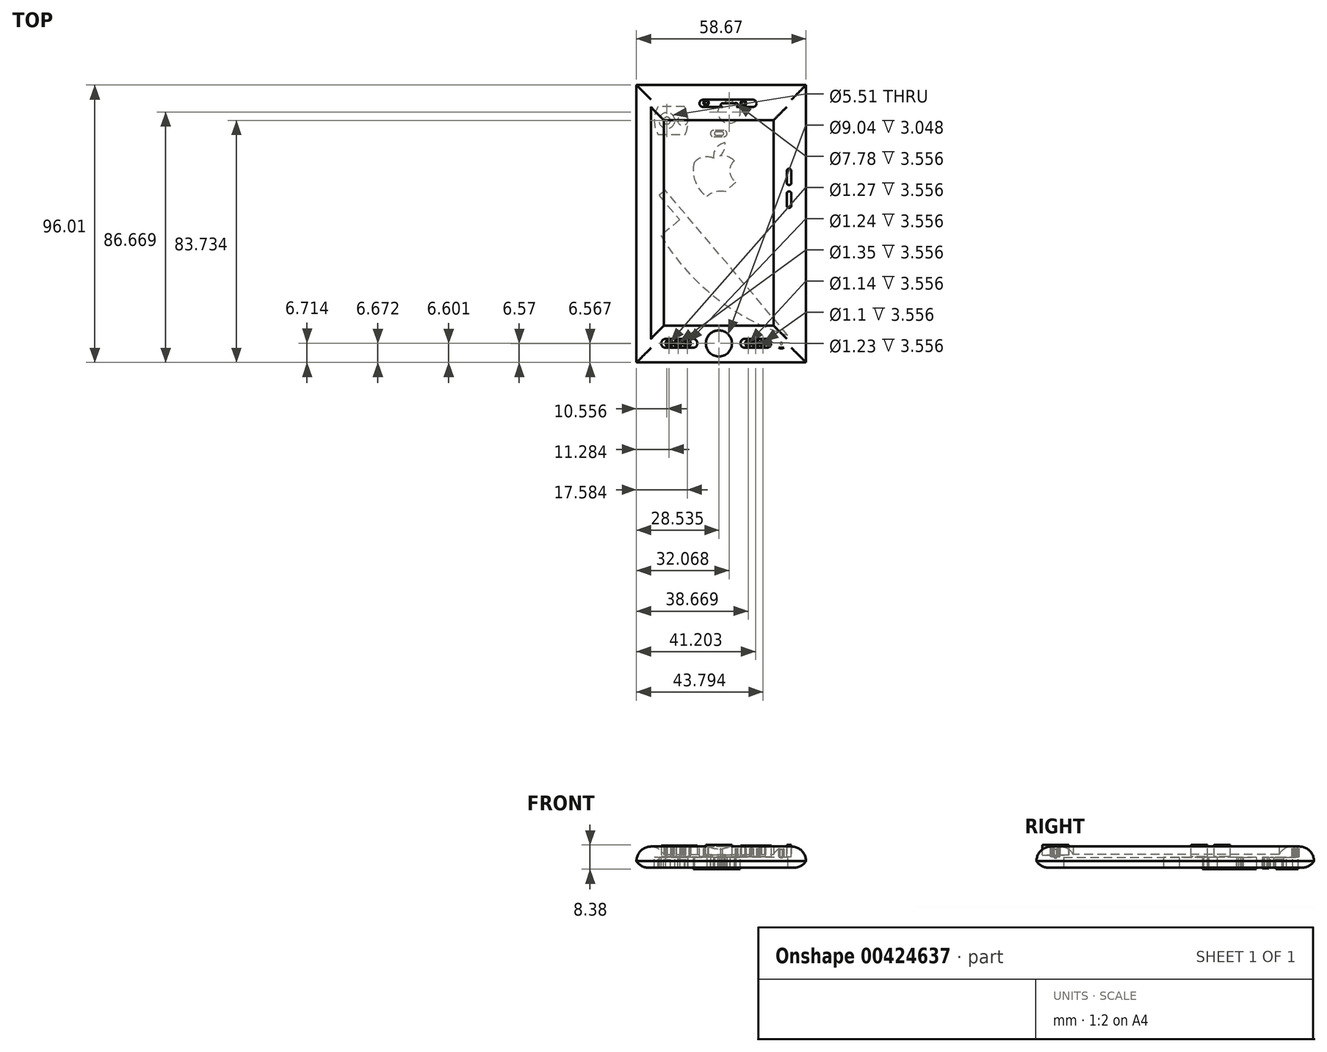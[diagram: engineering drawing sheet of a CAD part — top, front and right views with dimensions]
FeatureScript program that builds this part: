
annotation { "Feature Type Name" : "Feature", "Feature Type Description" : "" }
export const myFeature = defineFeature(function(context is Context, id is Id, definition is map)
    precondition{}
    {
        {
            var Q0;
            Q0=qCreatedBy(makeId("Top.planeOp"),FACE);
            var sketch = newSketch(context, id + "F0", { "sketchPlane" : qUnion([Q0])});
            skLineSegment(sketch, "E0", {"start": v(31.94, 80.74) * mm, "end": v(31.94, -15.27) * mm});
            skLineSegment(sketch, "E1", {"start": v(-26.73, 80.74) * mm, "end": v(-26.73, -15.27) * mm});
            skLineSegment(sketch, "E2", {"start": v(-26.73, -15.27) * mm, "end": v(31.94, -15.27) * mm});
            skLineSegment(sketch, "E3", {"start": v(31.94, 80.74) * mm, "end": v(-26.73, 80.74) * mm});
            skSolve(sketch);
        }
        {
            var Q0;
            Q0=makeQuery(id+"F0.imprint","IMPRINT",FACE,{"disambiguationData":[TD([[makeQuery(id+"F0.imprint","IMPRINT",EDGE,{"derivedFrom":sQuery(id+"F0.wireOp",EDGE,"E0")}),-1.0]])]});
            extrude(context, id + "F1", {"entities" : qUnion([Q0]), "depth" : 7.37 * mm});
        }
        {
            var Q0;
            Q0=makeQuery(id+"F1.opExtrude","CAP_FACE",FACE,{"disambiguationData":[OSD([sQuery(id+"F0.wireOp",EDGE,"E0"),sQuery(id+"F0.wireOp",EDGE,"E1"),sQuery(id+"F0.wireOp",EDGE,"E2"),sQuery(id+"F0.wireOp",EDGE,"E3")])],"isStart":false});
            var sketch = newSketch(context, id + "F2", { "sketchPlane" : qUnion([Q0])});
            skLineSegment(sketch, "E4.bottom", {"start": v(-17.26, 68.64) * mm, "end": v(20.73, 68.64) * mm});
            skLineSegment(sketch, "E4.top", {"start": v(-17.26, -2.55) * mm, "end": v(20.73, -2.55) * mm});
            skLineSegment(sketch, "E4.left", {"start": v(-17.26, 68.64) * mm, "end": v(-17.26, -2.55) * mm});
            skLineSegment(sketch, "E4.right", {"start": v(20.73, 68.64) * mm, "end": v(20.73, -2.55) * mm});
            skSolve(sketch);
        }
        {
            var Q0;
            Q0=makeQuery(id+"F2.imprint","IMPRINT",FACE,{"disambiguationData":[TD([[makeQuery(id+"F2.imprint","IMPRINT",EDGE,{"derivedFrom":sQuery(id+"F2.wireOp",EDGE,"E4.bottom")}),-1.0]])]});
            extrude(context, id + "F3", {"entities" : qUnion([Q0]), "operationType" : NewBodyOperationType.REMOVE, "oppositeDirection" : true, "depth" : 2.8 * mm});
        }
        {
            var Q0;
            Q0=makeQuery(id+"F3.boolean.opBoolean","COPY",FACE,{"derivedFrom":makeQuery(id+"F3.opExtrude","CAP_FACE",FACE,{"disambiguationData":[OSD([sQuery(id+"F2.wireOp",EDGE,"E4.bottom"),sQuery(id+"F2.wireOp",EDGE,"E4.top"),sQuery(id+"F2.wireOp",EDGE,"E4.left"),sQuery(id+"F2.wireOp",EDGE,"E4.right")])],"isStart":false})});
            extrude(context, id + "F4", {"entities" : qUnion([Q0]), "depth" : 2.8 * mm});
        }
        {
            var Q0;
            Q0=makeQuery(id+"F1.opExtrude","CAP_FACE",FACE,{"disambiguationData":[OSD([sQuery(id+"F0.wireOp",EDGE,"E0"),sQuery(id+"F0.wireOp",EDGE,"E1"),sQuery(id+"F0.wireOp",EDGE,"E2"),sQuery(id+"F0.wireOp",EDGE,"E3")])],"isStart":false});
            fillet(context, id + "F5", {"entities" : qUnion([Q0]), "radius" : 5.08 * mm, "tangentPropagation" : true, "allowEdgeOverflow" : false});
        }
        {
            var Q0;
            Q0=makeQuery(id+"F1.opExtrude","CAP_FACE",FACE,{"disambiguationData":[OSD([sQuery(id+"F0.wireOp",EDGE,"E0"),sQuery(id+"F0.wireOp",EDGE,"E1"),sQuery(id+"F0.wireOp",EDGE,"E2"),sQuery(id+"F0.wireOp",EDGE,"E3")])],"isStart":true});
            fillet(context, id + "F6", {"entities" : qUnion([Q0]), "radius" : 5.08 * mm, "tangentPropagation" : true, "allowEdgeOverflow" : false});
        }
        {
            var Q0;
            Q0=makeQuery(id+"F1.opExtrude","CAP_FACE",FACE,{"disambiguationData":[OSD([sQuery(id+"F0.wireOp",EDGE,"E0"),sQuery(id+"F0.wireOp",EDGE,"E1"),sQuery(id+"F0.wireOp",EDGE,"E2"),sQuery(id+"F0.wireOp",EDGE,"E3")])],"isStart":false});
            var sketch = newSketch(context, id + "F7", { "sketchPlane" : qUnion([Q0])});
            skCircle(sketch, "E5", {"center": v(1.8, -8.67) * mm, "radius": 4.52 * mm});
            skSolve(sketch);
        }
        {
            var Q0;
            Q0 = qSketchRegion(id + "F7", true);
            extrude(context, id + "F8", {"entities" : qUnion([Q0]), "operationType" : NewBodyOperationType.REMOVE, "oppositeDirection" : true, "depth" : 3.05 * mm});
        }
        {
            var Q0;
            Q0=makeQuery(id+"F8.boolean.opBoolean","COPY",FACE,{"derivedFrom":makeQuery(id+"F8.opExtrude","CAP_FACE",FACE,{"disambiguationData":[OSD([sQuery(id+"F7.wireOp",EDGE,"E5")])],"isStart":false})});
            extrude(context, id + "F9", {"entities" : qUnion([Q0]), "depth" : 3.56 * mm});
        }
        {
            var Q0;
            Q0=makeQuery(id+"F1.opExtrude","CAP_FACE",FACE,{"disambiguationData":[OSD([sQuery(id+"F0.wireOp",EDGE,"E0"),sQuery(id+"F0.wireOp",EDGE,"E1"),sQuery(id+"F0.wireOp",EDGE,"E2"),sQuery(id+"F0.wireOp",EDGE,"E3")])],"isStart":true});
            var sketch = newSketch(context, id + "F10", { "sketchPlane" : qUnion([Q0])});
            skLineSegment(sketch, "E6", {"start": v(25.58, 5.84) * mm, "end": v(4.61, -18.99) * mm});
            skLineSegment(sketch, "E7", {"start": v(4.61, -18.99) * mm, "end": v(-4.3, -29.54) * mm});
            skLineSegment(sketch, "E8", {"start": v(-4.3, -29.54) * mm, "end": v(-9.77, -36.03) * mm});
            skLineSegment(sketch, "E9", {"start": v(-9.77, -36.03) * mm, "end": v(-16.77, -44.32) * mm});
            skLineSegment(sketch, "E10", {"start": v(-16.77, -44.32) * mm, "end": v(-18.9, -42.52) * mm});
            skLineSegment(sketch, "E11", {"start": v(-18.9, -42.52) * mm, "end": v(-11.81, -34.13) * mm});
            skLineSegment(sketch, "E12", {"start": v(-11.81, -34.13) * mm, "end": v(-18.28, -28.67) * mm});
            skArc(sketch, "E13", {"start": v(25.58, 5.84) * mm, "mid": v(0.46, -7.36) * mm, "end": v(-18.28, -28.67) * mm});
            skSolve(sketch);
        }
        {
            var Q0;
            Q0 = qSketchRegion(id + "F10", true);
            extrude(context, id + "F11", {"entities" : qUnion([Q0]), "operationType" : NewBodyOperationType.REMOVE, "oppositeDirection" : true, "depth" : 3.56 * mm});
        }
        {
            var Q0;
            Q0=makeQuery(id+"F11.boolean.opBoolean","COPY",FACE,{"derivedFrom":makeQuery(id+"F11.opExtrude","CAP_FACE",FACE,{"disambiguationData":[OSD([sQuery(id+"F10.wireOp",EDGE,"E6"),sQuery(id+"F10.wireOp",EDGE,"E7"),sQuery(id+"F10.wireOp",EDGE,"E8"),sQuery(id+"F10.wireOp",EDGE,"E9"),sQuery(id+"F10.wireOp",EDGE,"E10"),sQuery(id+"F10.wireOp",EDGE,"E11"),sQuery(id+"F10.wireOp",EDGE,"E12"),sQuery(id+"F10.wireOp",EDGE,"E13")])],"isStart":false})});
            extrude(context, id + "F12", {"entities" : qUnion([Q0]), "depth" : 3.56 * mm});
        }
        {
            var Q0;
            Q0=qCreatedBy(makeId("Top.planeOp"),FACE);
            var sketch = newSketch(context, id + "F13", { "sketchPlane" : qUnion([Q0])});
            skArc(sketch, "E14", {"start": v(7.09, 54.53) * mm, "mid": v(5.57, 50.71) * mm, "end": v(7.7, 47.2) * mm});
            skArc(sketch, "E15", {"start": v(7.09, 54.53) * mm, "mid": v(3.7, 56.23) * mm, "end": v(0, 55.38) * mm});
            skArc(sketch, "E16", {"start": v(0, 55.38) * mm, "mid": v(-3.61, 55.8) * mm, "end": v(-6.74, 53.95) * mm});
            skArc(sketch, "E17", {"start": v(-6.74, 53.95) * mm, "mid": v(-6.38, 47.38) * mm, "end": v(-2.37, 42.16) * mm});
            skArc(sketch, "E18", {"start": v(3.93, 43.83) * mm, "mid": v(0.57, 43.76) * mm, "end": v(-2.37, 42.16) * mm});
            skLineSegment(sketch, "E19", {"start": v(7.7, 47.2) * mm, "end": v(3.93, 43.83) * mm});
            skArc(sketch, "E20", {"start": v(0, 55.38) * mm, "mid": v(3.12, 57.25) * mm, "end": v(3.87, 60.8) * mm});
            skArc(sketch, "E21", {"start": v(3.87, 60.8) * mm, "mid": v(0.85, 58.87) * mm, "end": v(0, 55.38) * mm});
            skSolve(sketch);
        }
        {
            var Q0;
            {var subQ0=sQuery(id+"F13.wireOp",EDGE,"E21");Q0=makeQuery(id+"F13.imprint","IMPRINT",FACE,{"disambiguationData":[TD([[makeQuery(id+"F13.imprint","IMPRINT",EDGE,{"derivedFrom":subQ0}),1.0]])]});}
            var Q1;
            {var subQ0=sQuery(id+"F13.wireOp",EDGE,"E20");var subQ1=sQuery(id+"F13.wireOp",EDGE,"E15");var subQ3=makeQuery(id+"F13.imprint","INTERSECT",VERTEX,{"derivedFrom":[subQ1,subQ0]});Q1=makeQuery(id+"F13.imprint","IMPRINT",FACE,{"disambiguationData":[TD([[makeQuery(id+"F13.imprint","IMPRINT",EDGE,{"disambiguationData":[TD([[subQ3,-1.0]])],"derivedFrom":subQ1}),1.0]])]});}
            var Q2;
            {var subQ2=sQuery(id+"F13.wireOp",EDGE,"E14");Q2=makeQuery(id+"F13.imprint","IMPRINT",FACE,{"disambiguationData":[TD([[makeQuery(id+"F13.imprint","IMPRINT",EDGE,{"derivedFrom":subQ2}),-1.0]])]});}
            extrude(context, id + "F14", {"entities" : qUnion([Q0, Q1, Q2]), "operationType" : NewBodyOperationType.REMOVE, "depth" : 3.56 * mm});
        }
        {
            var Q0;
            Q0=makeQuery(id+"F14.boolean.opBoolean","COPY",FACE,{"derivedFrom":makeQuery(id+"F14.opExtrude","CAP_FACE",FACE,{"disambiguationData":[OSD([sQuery(id+"F13.wireOp",EDGE,"E14"),sQuery(id+"F13.wireOp",EDGE,"E15"),sQuery(id+"F13.wireOp",EDGE,"E16"),sQuery(id+"F13.wireOp",EDGE,"E17"),sQuery(id+"F13.wireOp",EDGE,"E18"),sQuery(id+"F13.wireOp",EDGE,"E19"),sQuery(id+"F13.wireOp",EDGE,"E20"),sQuery(id+"F13.wireOp",EDGE,"E21")])],"isStart":false})});
            extrude(context, id + "F15", {"entities" : qUnion([Q0]), "depth" : 4.06 * mm});
        }
        {
            var Q0;
            Q0=makeQuery(id+"F1.opExtrude","CAP_FACE",FACE,{"disambiguationData":[OSD([sQuery(id+"F0.wireOp",EDGE,"E0"),sQuery(id+"F0.wireOp",EDGE,"E1"),sQuery(id+"F0.wireOp",EDGE,"E2"),sQuery(id+"F0.wireOp",EDGE,"E3")])],"isStart":true});
            var sketch = newSketch(context, id + "F16", { "sketchPlane" : qUnion([Q0])});
            skLineSegment(sketch, "E22", {"start": v(-10.1, -73.34) * mm, "end": v(-19.28, -73.34) * mm});
            skArc(sketch, "E23", {"start": v(-19.28, -63.67) * mm, "mid": v(-20.55, -68.5) * mm, "end": v(-19.28, -73.34) * mm});
            skLineSegment(sketch, "E24", {"start": v(-19.28, -63.67) * mm, "end": v(-9.78, -63.67) * mm});
            skArc(sketch, "E25", {"start": v(-10.1, -73.34) * mm, "mid": v(-8.86, -68.49) * mm, "end": v(-9.88, -63.58) * mm});
            skCircle(sketch, "E26", {"center": v(-16.17, -68.46) * mm, "radius": 2.75 * mm});
            skCircle(sketch, "E27", {"center": v(-16.17, -68.46) * mm, "radius": 1.6 * mm});
            skCircle(sketch, "E28", {"center": v(-10.69, -68.5) * mm, "radius": 1.76 * mm});
            skSolve(sketch);
        }
        {
            var Q0;
            Q0 = qSketchRegion(id + "F16", true);
            extrude(context, id + "F17", {"entities" : qUnion([Q0]), "operationType" : NewBodyOperationType.REMOVE, "oppositeDirection" : true, "depth" : 3.56 * mm});
        }
        {
            var Q0;
            Q0=makeQuery(id+"F17.boolean.opBoolean","COPY",FACE,{"derivedFrom":makeQuery(id+"F17.opExtrude","CAP_FACE",FACE,{"disambiguationData":[OSD([sQuery(id+"F16.wireOp",EDGE,"E22"),sQuery(id+"F16.wireOp",EDGE,"E23"),sQuery(id+"F16.wireOp",EDGE,"E24"),sQuery(id+"F16.wireOp",EDGE,"E25"),sQuery(id+"F16.wireOp",EDGE,"E26"),sQuery(id+"F16.wireOp",EDGE,"E28")])],"isStart":false})});
            extrude(context, id + "F18", {"entities" : qUnion([Q0]), "depth" : 3.56 * mm});
        }
        {
            var Q0;
            Q0=makeQuery(id+"F17.boolean.opBoolean","SPLIT",FACE,{"disambiguationData":[TD([makeQuery(id+"F17.opExtrude","SWEPT_FACE",FACE,{"disambiguationData":[OSD([sQuery(id+"F16.wireOp",EDGE,"E26")])]})])],"derivedFrom":makeQuery(id+"F1.opExtrude","CAP_FACE",FACE,{"disambiguationData":[OSD([sQuery(id+"F0.wireOp",EDGE,"E0"),sQuery(id+"F0.wireOp",EDGE,"E1"),sQuery(id+"F0.wireOp",EDGE,"E2"),sQuery(id+"F0.wireOp",EDGE,"E3")])],"isStart":true})});
            var sketch = newSketch(context, id + "F19", { "sketchPlane" : qUnion([Q0])});
            skCircle(sketch, "E29", {"center": v(-16.17, -68.46) * mm, "radius": 1.23 * mm});
            skCircle(sketch, "E30", {"center": v(-10.43, -68.62) * mm, "radius": 1.64 * mm});
            skSolve(sketch);
        }
        {
            var Q0;
            Q0=makeQuery(id+"F19.imprint","IMPRINT",FACE,{"disambiguationData":[TD([[makeQuery(id+"F19.imprint","IMPRINT",EDGE,{"derivedFrom":sQuery(id+"F19.wireOp",EDGE,"E29")}),1.0]])]});
            extrude(context, id + "F20", {"entities" : qUnion([Q0]), "operationType" : NewBodyOperationType.REMOVE, "oppositeDirection" : true, "depth" : 2.8 * mm});
        }
        {
            var Q0;
            Q0=makeQuery(id+"F20.boolean.opBoolean","COPY",FACE,{"derivedFrom":makeQuery(id+"F20.opExtrude","CAP_FACE",FACE,{"disambiguationData":[OSD([sQuery(id+"F19.wireOp",EDGE,"E29")])],"isStart":false})});
            extrude(context, id + "F21", {"entities" : qUnion([Q0]), "depth" : 2.8 * mm});
        }
        {
            var Q0;
            Q0=makeQuery(id+"F17.boolean.opBoolean","SPLIT",FACE,{"disambiguationData":[TD([makeQuery(id+"F17.opExtrude","SWEPT_FACE",FACE,{"disambiguationData":[OSD([sQuery(id+"F16.wireOp",EDGE,"E28")])]})])],"derivedFrom":makeQuery(id+"F1.opExtrude","CAP_FACE",FACE,{"disambiguationData":[OSD([sQuery(id+"F0.wireOp",EDGE,"E0"),sQuery(id+"F0.wireOp",EDGE,"E1"),sQuery(id+"F0.wireOp",EDGE,"E2"),sQuery(id+"F0.wireOp",EDGE,"E3")])],"isStart":true})});
            extrude(context, id + "F22", {"entities" : qUnion([Q0]), "operationType" : NewBodyOperationType.REMOVE, "oppositeDirection" : true, "depth" : 2.8 * mm});
        }
        {
            var Q0;
            Q0=makeQuery(id+"F22.boolean.opBoolean","COPY",FACE,{"derivedFrom":makeQuery(id+"F22.opExtrude","CAP_FACE",FACE,{"disambiguationData":[OSD([sQuery(id+"F0.wireOp",EDGE,"E0"),sQuery(id+"F0.wireOp",EDGE,"E1"),sQuery(id+"F0.wireOp",EDGE,"E2"),sQuery(id+"F0.wireOp",EDGE,"E3")])],"isStart":false})});
            extrude(context, id + "F23", {"entities" : qUnion([Q0]), "depth" : 2.8 * mm});
        }
        {
            var Q0;
            {var subQ0=sQuery(id+"F0.wireOp",EDGE,"E3");var subQ1=sQuery(id+"F0.wireOp",EDGE,"E2");var subQ2=sQuery(id+"F0.wireOp",EDGE,"E1");var subQ3=sQuery(id+"F0.wireOp",EDGE,"E0");Q0=makeQuery(id+"F8.boolean.opBoolean","SPLIT",FACE,{"disambiguationData":[TD([makeQuery(id+"F5.opFillet","BLEND_FACE",FACE,{"disambiguationData":[OSD([subQ3])]}),makeQuery(id+"F5.opFillet","BLEND_FACE",FACE,{"disambiguationData":[OSD([subQ2])]}),makeQuery(id+"F5.opFillet","BLEND_FACE",FACE,{"disambiguationData":[OSD([subQ1])]}),makeQuery(id+"F5.opFillet","BLEND_FACE",FACE,{"disambiguationData":[OSD([subQ0])]}),makeQuery(id+"F5.opFillet","BLEND_FACE",FACE,{"disambiguationData":[OSD([sQuery(id+"F2.wireOp",EDGE,"E4.bottom")])]}),makeQuery(id+"F5.opFillet","BLEND_FACE",FACE,{"disambiguationData":[OSD([sQuery(id+"F2.wireOp",EDGE,"E4.top")])]}),makeQuery(id+"F5.opFillet","BLEND_FACE",FACE,{"disambiguationData":[OSD([sQuery(id+"F2.wireOp",EDGE,"E4.right")])]}),makeQuery(id+"F8.opExtrude","SWEPT_FACE",FACE,{"disambiguationData":[OSD([sQuery(id+"F7.wireOp",EDGE,"E5")])]})])],"derivedFrom":makeQuery(id+"F1.opExtrude","CAP_FACE",FACE,{"disambiguationData":[OSD([subQ3,subQ2,subQ1,subQ0])],"isStart":false})});}
            var sketch = newSketch(context, id + "F24", { "sketchPlane" : qUnion([Q0])});
            skLineSegment(sketch, "E31", {"start": v(-3.7, 75.66) * mm, "end": v(13.59, 75.66) * mm});
            skArc(sketch, "E32", {"start": v(13.59, 73.18) * mm, "mid": v(14.83, 74.42) * mm, "end": v(13.59, 75.66) * mm});
            skLineSegment(sketch, "E33", {"start": v(13.59, 73.18) * mm, "end": v(-3.7, 73.18) * mm});
            skArc(sketch, "E34", {"start": v(-3.7, 75.66) * mm, "mid": v(-4.94, 74.42) * mm, "end": v(-3.7, 73.18) * mm});
            skCircle(sketch, "E35", {"center": v(-2.62, 74.6) * mm, "radius": 0.93 * mm});
            skLineSegment(sketch, "E36", {"start": v(3.14, 74.5) * mm, "end": v(7.53, 74.5) * mm});
            skArc(sketch, "E37", {"start": v(7.53, 73.18) * mm, "mid": v(8.4, 73.84) * mm, "end": v(7.53, 74.5) * mm});
            skLineSegment(sketch, "E38", {"start": v(7.53, 73.18) * mm, "end": v(3.14, 73.18) * mm});
            skArc(sketch, "E39", {"start": v(3.14, 74.5) * mm, "mid": v(2.48, 73.84) * mm, "end": v(3.14, 73.18) * mm});
            skCircle(sketch, "E40", {"center": v(10.27, 74.5) * mm, "radius": 1 * mm});
            skSolve(sketch);
        }
        {
            var Q0;
            Q0=makeQuery(id+"F24.imprint","IMPRINT",FACE,{"disambiguationData":[TD([[makeQuery(id+"F24.imprint","IMPRINT",EDGE,{"derivedFrom":sQuery(id+"F24.wireOp",EDGE,"E31")}),1.0]])]});
            extrude(context, id + "F25", {"entities" : qUnion([Q0]), "operationType" : NewBodyOperationType.REMOVE, "oppositeDirection" : true, "depth" : 3.56 * mm});
        }
        {
            var Q0;
            Q0=makeQuery(id+"F25.boolean.opBoolean","COPY",FACE,{"derivedFrom":makeQuery(id+"F25.opExtrude","CAP_FACE",FACE,{"disambiguationData":[OSD([sQuery(id+"F24.wireOp",EDGE,"E31"),sQuery(id+"F24.wireOp",EDGE,"E32"),sQuery(id+"F24.wireOp",EDGE,"E33"),sQuery(id+"F24.wireOp",EDGE,"E34"),sQuery(id+"F24.wireOp",EDGE,"E35"),sQuery(id+"F24.wireOp",EDGE,"E36"),sQuery(id+"F24.wireOp",EDGE,"E37"),sQuery(id+"F24.wireOp",EDGE,"E39"),sQuery(id+"F24.wireOp",EDGE,"E40")])],"isStart":false})});
            extrude(context, id + "F26", {"entities" : qUnion([Q0]), "depth" : 3.56 * mm});
        }
        {
            var Q0;
            {var subQ0=sQuery(id+"F0.wireOp",EDGE,"E3");var subQ1=sQuery(id+"F0.wireOp",EDGE,"E2");var subQ2=sQuery(id+"F0.wireOp",EDGE,"E1");var subQ3=sQuery(id+"F0.wireOp",EDGE,"E0");Q0=makeQuery(id+"F25.boolean.opBoolean","SPLIT",FACE,{"disambiguationData":[TD([makeQuery(id+"F25.opExtrude","SWEPT_FACE",FACE,{"disambiguationData":[OSD([sQuery(id+"F24.wireOp",EDGE,"E35")])]})])],"derivedFrom":makeQuery(id+"F8.boolean.opBoolean","SPLIT",FACE,{"disambiguationData":[TD([makeQuery(id+"F5.opFillet","BLEND_FACE",FACE,{"disambiguationData":[OSD([subQ3])]}),makeQuery(id+"F5.opFillet","BLEND_FACE",FACE,{"disambiguationData":[OSD([subQ2])]}),makeQuery(id+"F5.opFillet","BLEND_FACE",FACE,{"disambiguationData":[OSD([subQ1])]}),makeQuery(id+"F5.opFillet","BLEND_FACE",FACE,{"disambiguationData":[OSD([subQ0])]}),makeQuery(id+"F5.opFillet","BLEND_FACE",FACE,{"disambiguationData":[OSD([sQuery(id+"F2.wireOp",EDGE,"E4.bottom")])]}),makeQuery(id+"F5.opFillet","BLEND_FACE",FACE,{"disambiguationData":[OSD([sQuery(id+"F2.wireOp",EDGE,"E4.top")])]}),makeQuery(id+"F5.opFillet","BLEND_FACE",FACE,{"disambiguationData":[OSD([sQuery(id+"F2.wireOp",EDGE,"E4.right")])]}),makeQuery(id+"F8.opExtrude","SWEPT_FACE",FACE,{"disambiguationData":[OSD([sQuery(id+"F7.wireOp",EDGE,"E5")])]})])],"derivedFrom":makeQuery(id+"F1.opExtrude","CAP_FACE",FACE,{"disambiguationData":[OSD([subQ3,subQ2,subQ1,subQ0])],"isStart":false})})});}
            var sketch = newSketch(context, id + "F27", { "sketchPlane" : qUnion([Q0])});
            skCircle(sketch, "E41", {"center": v(-2.62, 74.6) * mm, "radius": 0.57 * mm});
            skSolve(sketch);
        }
        {
            var Q0;
            Q0 = qSketchRegion(id + "F27", true);
            extrude(context, id + "F28", {"entities" : qUnion([Q0]), "operationType" : NewBodyOperationType.REMOVE, "oppositeDirection" : true, "depth" : 3.05 * mm});
        }
        {
            var Q0;
            Q0=makeQuery(id+"F28.boolean.opBoolean","COPY",FACE,{"derivedFrom":makeQuery(id+"F28.opExtrude","CAP_FACE",FACE,{"disambiguationData":[OSD([sQuery(id+"F27.wireOp",EDGE,"E41")])],"isStart":false})});
            extrude(context, id + "F29", {"entities" : qUnion([Q0]), "depth" : 3.05 * mm});
        }
        {
            var Q0;
            {var subQ0=sQuery(id+"F0.wireOp",EDGE,"E3");var subQ1=sQuery(id+"F0.wireOp",EDGE,"E2");var subQ2=sQuery(id+"F0.wireOp",EDGE,"E1");var subQ3=sQuery(id+"F0.wireOp",EDGE,"E0");Q0=makeQuery(id+"F25.boolean.opBoolean","SPLIT",FACE,{"disambiguationData":[TD([makeQuery(id+"F25.opExtrude","SWEPT_FACE",FACE,{"disambiguationData":[OSD([sQuery(id+"F24.wireOp",EDGE,"E40")])]})])],"derivedFrom":makeQuery(id+"F8.boolean.opBoolean","SPLIT",FACE,{"disambiguationData":[TD([makeQuery(id+"F5.opFillet","BLEND_FACE",FACE,{"disambiguationData":[OSD([subQ3])]}),makeQuery(id+"F5.opFillet","BLEND_FACE",FACE,{"disambiguationData":[OSD([subQ2])]}),makeQuery(id+"F5.opFillet","BLEND_FACE",FACE,{"disambiguationData":[OSD([subQ1])]}),makeQuery(id+"F5.opFillet","BLEND_FACE",FACE,{"disambiguationData":[OSD([subQ0])]}),makeQuery(id+"F5.opFillet","BLEND_FACE",FACE,{"disambiguationData":[OSD([sQuery(id+"F2.wireOp",EDGE,"E4.bottom")])]}),makeQuery(id+"F5.opFillet","BLEND_FACE",FACE,{"disambiguationData":[OSD([sQuery(id+"F2.wireOp",EDGE,"E4.top")])]}),makeQuery(id+"F5.opFillet","BLEND_FACE",FACE,{"disambiguationData":[OSD([sQuery(id+"F2.wireOp",EDGE,"E4.right")])]}),makeQuery(id+"F8.opExtrude","SWEPT_FACE",FACE,{"disambiguationData":[OSD([sQuery(id+"F7.wireOp",EDGE,"E5")])]})])],"derivedFrom":makeQuery(id+"F1.opExtrude","CAP_FACE",FACE,{"disambiguationData":[OSD([subQ3,subQ2,subQ1,subQ0])],"isStart":false})})});}
            var sketch = newSketch(context, id + "F30", { "sketchPlane" : qUnion([Q0])});
            skCircle(sketch, "E42", {"center": v(10.27, 74.5) * mm, "radius": 0.57 * mm});
            skSolve(sketch);
        }
        {
            var Q0;
            Q0 = qSketchRegion(id + "F30", true);
            extrude(context, id + "F31", {"entities" : qUnion([Q0]), "operationType" : NewBodyOperationType.REMOVE, "oppositeDirection" : true, "depth" : 3.05 * mm});
        }
        {
            var Q0;
            Q0=makeQuery(id+"F31.boolean.opBoolean","COPY",FACE,{"derivedFrom":makeQuery(id+"F31.opExtrude","CAP_FACE",FACE,{"disambiguationData":[OSD([sQuery(id+"F30.wireOp",EDGE,"E42")])],"isStart":false})});
            extrude(context, id + "F32", {"entities" : qUnion([Q0]), "depth" : 3.05 * mm});
        }
        {
            var Q0;
            {var subQ0=sQuery(id+"F0.wireOp",EDGE,"E0");var subQ1=sQuery(id+"F0.wireOp",EDGE,"E1");var subQ2=sQuery(id+"F0.wireOp",EDGE,"E2");var subQ3=sQuery(id+"F0.wireOp",EDGE,"E3");Q0=makeQuery(id+"F17.boolean.opBoolean","SPLIT",FACE,{"disambiguationData":[TD([makeQuery(id+"F6.opFillet","BLEND_FACE",FACE,{"disambiguationData":[OSD([subQ0])]})])],"derivedFrom":makeQuery(id+"F1.opExtrude","CAP_FACE",FACE,{"disambiguationData":[OSD([subQ0,subQ1,subQ2,subQ3])],"isStart":true})});}
            var sketch = newSketch(context, id + "F33", { "sketchPlane" : qUnion([Q0])});
            skCircle(sketch, "E43", {"center": v(5.34, -71.4) * mm, "radius": 3.9 * mm});
            skSolve(sketch);
        }
        {
            var Q0;
            Q0 = qSketchRegion(id + "F33", true);
            extrude(context, id + "F34", {"entities" : qUnion([Q0]), "operationType" : NewBodyOperationType.REMOVE, "oppositeDirection" : true, "depth" : 3.56 * mm});
        }
        {
            var Q0;
            Q0=makeQuery(id+"F34.boolean.opBoolean","COPY",FACE,{"derivedFrom":makeQuery(id+"F34.opExtrude","CAP_FACE",FACE,{"disambiguationData":[OSD([sQuery(id+"F33.wireOp",EDGE,"E43")])],"isStart":false})});
            extrude(context, id + "F35", {"entities" : qUnion([Q0]), "depth" : 4.06 * mm});
        }
        {
            var Q0;
            {var subQ0=sQuery(id+"F2.wireOp",EDGE,"E4.bottom");var subQ1=makeQuery(id+"F5.opFillet","BLEND_FACE",FACE,{"disambiguationData":[OSD([subQ0])]});var subQ2=sQuery(id+"F0.wireOp",EDGE,"E3");var subQ3=makeQuery(id+"F5.opFillet","BLEND_FACE",FACE,{"disambiguationData":[OSD([subQ2])]});var subQ4=sQuery(id+"F0.wireOp",EDGE,"E2");var subQ5=makeQuery(id+"F5.opFillet","BLEND_FACE",FACE,{"disambiguationData":[OSD([subQ4])]});var subQ6=sQuery(id+"F0.wireOp",EDGE,"E0");var subQ7=makeQuery(id+"F5.opFillet","BLEND_FACE",FACE,{"disambiguationData":[OSD([subQ6])]});var subQ8=makeQuery(id+"F5.opFillet","BLEND_FACE",FACE,{"disambiguationData":[OSD([sQuery(id+"F2.wireOp",EDGE,"E4.top")])]});var subQ9=makeQuery(id+"F5.opFillet","BLEND_FACE",FACE,{"disambiguationData":[OSD([sQuery(id+"F2.wireOp",EDGE,"E4.right")])]});var subQ10=makeQuery(id+"F8.opExtrude","SWEPT_FACE",FACE,{"disambiguationData":[OSD([sQuery(id+"F7.wireOp",EDGE,"E5")])]});var subQ13=sQuery(id+"F0.wireOp",EDGE,"E1");var subQ14=makeQuery(id+"F1.opExtrude","CAP_FACE",FACE,{"disambiguationData":[OSD([subQ6,subQ13,subQ4,subQ2])],"isStart":false});Q0=makeQuery(id+"F25.boolean.opBoolean","SPLIT",FACE,{"disambiguationData":[TD([subQ7])],"derivedFrom":makeQuery(id+"F8.boolean.opBoolean","SPLIT",FACE,{"disambiguationData":[TD([subQ7,makeQuery(id+"F5.opFillet","BLEND_FACE",FACE,{"disambiguationData":[OSD([subQ13])]}),subQ5,subQ3,subQ1,subQ8,subQ9,subQ10])],"derivedFrom":subQ14})});}
            var sketch = newSketch(context, id + "F36", { "sketchPlane" : qUnion([Q0])});
            skLineSegment(sketch, "E44", {"start": v(26.86, 51) * mm, "end": v(26.86, 46.94) * mm});
            skArc(sketch, "E45", {"start": v(25.27, 46.94) * mm, "mid": v(26.07, 46.15) * mm, "end": v(26.86, 46.94) * mm});
            skLineSegment(sketch, "E46.bottom", {"start": v(25.27, 46.94) * mm, "end": v(25.27, 46.94) * mm});
            skLineSegment(sketch, "E46.top", {"start": v(25.27, 51) * mm, "end": v(25.27, 51) * mm});
            skLineSegment(sketch, "E46.left", {"start": v(25.27, 46.94) * mm, "end": v(25.27, 51) * mm});
            skLineSegment(sketch, "E46.right", {"start": v(25.27, 46.94) * mm, "end": v(25.27, 51) * mm});
            skArc(sketch, "E47", {"start": v(26.86, 51) * mm, "mid": v(26.07, 51.8) * mm, "end": v(25.27, 51) * mm});
            skSolve(sketch);
        }
        {
            var Q0;
            Q0=makeQuery(id+"F36.imprint","IMPRINT",FACE,{"disambiguationData":[TD([[makeQuery(id+"F36.imprint","IMPRINT",EDGE,{"derivedFrom":sQuery(id+"F36.wireOp",EDGE,"E44")}),1.0]])]});
            extrude(context, id + "F37", {"entities" : qUnion([Q0]), "operationType" : NewBodyOperationType.REMOVE, "oppositeDirection" : true, "depth" : 3.56 * mm});
        }
        {
            var Q0;
            Q0=makeQuery(id+"F37.boolean.opBoolean","COPY",FACE,{"derivedFrom":makeQuery(id+"F37.opExtrude","CAP_FACE",FACE,{"disambiguationData":[OSD([sQuery(id+"F36.wireOp",EDGE,"E44"),sQuery(id+"F36.wireOp",EDGE,"E45"),sQuery(id+"F36.wireOp",EDGE,"E46.right"),sQuery(id+"F36.wireOp",EDGE,"E47")])],"isStart":false})});
            extrude(context, id + "F38", {"entities" : qUnion([Q0]), "depth" : 4.06 * mm});
        }
        {
            var Q0;
            {var subQ0=makeQuery(id+"F5.opFillet","BLEND_FACE",FACE,{"disambiguationData":[OSD([sQuery(id+"F2.wireOp",EDGE,"E4.right")])]});var subQ1=sQuery(id+"F0.wireOp",EDGE,"E2");var subQ2=makeQuery(id+"F5.opFillet","BLEND_FACE",FACE,{"disambiguationData":[OSD([subQ1])]});var subQ3=makeQuery(id+"F5.opFillet","BLEND_FACE",FACE,{"disambiguationData":[OSD([sQuery(id+"F2.wireOp",EDGE,"E4.top")])]});var subQ4=sQuery(id+"F0.wireOp",EDGE,"E0");var subQ5=makeQuery(id+"F5.opFillet","BLEND_FACE",FACE,{"disambiguationData":[OSD([subQ4])]});var subQ6=makeQuery(id+"F8.opExtrude","SWEPT_FACE",FACE,{"disambiguationData":[OSD([sQuery(id+"F7.wireOp",EDGE,"E5")])]});var subQ8=sQuery(id+"F2.wireOp",EDGE,"E4.bottom");var subQ9=makeQuery(id+"F5.opFillet","BLEND_FACE",FACE,{"disambiguationData":[OSD([subQ8])]});var subQ10=sQuery(id+"F0.wireOp",EDGE,"E3");var subQ11=makeQuery(id+"F5.opFillet","BLEND_FACE",FACE,{"disambiguationData":[OSD([subQ10])]});var subQ14=sQuery(id+"F0.wireOp",EDGE,"E1");var subQ15=makeQuery(id+"F1.opExtrude","CAP_FACE",FACE,{"disambiguationData":[OSD([subQ4,subQ14,subQ1,subQ10])],"isStart":false});Q0=makeQuery(id+"F37.boolean.opBoolean","SPLIT",FACE,{"disambiguationData":[TD([subQ2])],"derivedFrom":makeQuery(id+"F25.boolean.opBoolean","SPLIT",FACE,{"disambiguationData":[TD([subQ5])],"derivedFrom":makeQuery(id+"F8.boolean.opBoolean","SPLIT",FACE,{"disambiguationData":[TD([subQ5,makeQuery(id+"F5.opFillet","BLEND_FACE",FACE,{"disambiguationData":[OSD([subQ14])]}),subQ2,subQ11,subQ9,subQ3,subQ0,subQ6])],"derivedFrom":subQ15})})});}
            var sketch = newSketch(context, id + "F39", { "sketchPlane" : qUnion([Q0])});
            skLineSegment(sketch, "E48", {"start": v(26.86, 43.14) * mm, "end": v(26.86, 39.03) * mm});
            skArc(sketch, "E49", {"start": v(25.27, 39.03) * mm, "mid": v(26.07, 38.23) * mm, "end": v(26.86, 39.03) * mm});
            skLineSegment(sketch, "E50", {"start": v(25.27, 39.03) * mm, "end": v(25.27, 43.14) * mm});
            skArc(sketch, "E51", {"start": v(26.86, 43.14) * mm, "mid": v(26.07, 43.94) * mm, "end": v(25.27, 43.14) * mm});
            skSolve(sketch);
        }
        {
            var Q0;
            Q0 = qSketchRegion(id + "F39", true);
            extrude(context, id + "F40", {"entities" : qUnion([Q0]), "operationType" : NewBodyOperationType.REMOVE, "oppositeDirection" : true, "depth" : 3.56 * mm});
        }
        {
            var Q0;
            Q0=makeQuery(id+"F40.boolean.opBoolean","COPY",FACE,{"derivedFrom":makeQuery(id+"F40.opExtrude","CAP_FACE",FACE,{"disambiguationData":[OSD([sQuery(id+"F39.wireOp",EDGE,"E48"),sQuery(id+"F39.wireOp",EDGE,"E49"),sQuery(id+"F39.wireOp",EDGE,"E50"),sQuery(id+"F39.wireOp",EDGE,"E51")])],"isStart":false})});
            extrude(context, id + "F41", {"entities" : qUnion([Q0]), "depth" : 4.06 * mm});
        }
        {
            var Q0;
            {var subQ0=sQuery(id+"F0.wireOp",EDGE,"E0");var subQ1=sQuery(id+"F0.wireOp",EDGE,"E1");var subQ2=sQuery(id+"F0.wireOp",EDGE,"E2");var subQ3=sQuery(id+"F0.wireOp",EDGE,"E3");Q0=makeQuery(id+"F17.boolean.opBoolean","SPLIT",FACE,{"disambiguationData":[TD([makeQuery(id+"F6.opFillet","BLEND_FACE",FACE,{"disambiguationData":[OSD([subQ0])]})])],"derivedFrom":makeQuery(id+"F1.opExtrude","CAP_FACE",FACE,{"disambiguationData":[OSD([subQ0,subQ1,subQ2,subQ3])],"isStart":true})});}
            var sketch = newSketch(context, id + "F42", { "sketchPlane" : qUnion([Q0])});
            skLineSegment(sketch, "E52", {"start": v(3.57, -65.08) * mm, "end": v(0, -65.08) * mm});
            skArc(sketch, "E53", {"start": v(0, -62.84) * mm, "mid": v(-1.12, -63.96) * mm, "end": v(0, -65.08) * mm});
            skLineSegment(sketch, "E54", {"start": v(0, -62.84) * mm, "end": v(3.46, -62.84) * mm});
            skArc(sketch, "E55", {"start": v(3.57, -65.08) * mm, "mid": v(4.58, -63.9) * mm, "end": v(3.46, -62.84) * mm});
            skLineSegment(sketch, "E56", {"start": v(2.78, -64.53) * mm, "end": v(0.77, -64.53) * mm});
            skArc(sketch, "E57", {"start": v(0.77, -63.42) * mm, "mid": v(0.22, -63.97) * mm, "end": v(0.77, -64.53) * mm});
            skLineSegment(sketch, "E58", {"start": v(0.77, -63.42) * mm, "end": v(2.7, -63.42) * mm});
            skArc(sketch, "E59", {"start": v(2.78, -64.53) * mm, "mid": v(3.46, -63.93) * mm, "end": v(2.7, -63.42) * mm});
            skSolve(sketch);
        }
        {
            var Q0;
            Q0 = qSketchRegion(id + "F42", true);
            extrude(context, id + "F43", {"entities" : qUnion([Q0]), "operationType" : NewBodyOperationType.REMOVE, "oppositeDirection" : true, "depth" : 3.56 * mm});
        }
        {
            var Q0;
            Q0=makeQuery(id+"F43.boolean.opBoolean","COPY",FACE,{"derivedFrom":makeQuery(id+"F43.opExtrude","CAP_FACE",FACE,{"disambiguationData":[OSD([sQuery(id+"F42.wireOp",EDGE,"E52"),sQuery(id+"F42.wireOp",EDGE,"E53"),sQuery(id+"F42.wireOp",EDGE,"E54"),sQuery(id+"F42.wireOp",EDGE,"E55"),sQuery(id+"F42.wireOp",EDGE,"E56"),sQuery(id+"F42.wireOp",EDGE,"E57"),sQuery(id+"F42.wireOp",EDGE,"E58"),sQuery(id+"F42.wireOp",EDGE,"E59")])],"isStart":false})});
            extrude(context, id + "F44", {"entities" : qUnion([Q0]), "depth" : 3.8 * mm});
        }
        {
            var Q0;
            {var subQ0=sQuery(id+"F0.wireOp",EDGE,"E1");var subQ1=sQuery(id+"F0.wireOp",EDGE,"E2");Q0=makeQuery(id+"F8.boolean.opBoolean","SPLIT",FACE,{"disambiguationData":[TD([makeQuery(id+"F5.opFillet","BLEND_FACE",FACE,{"disambiguationData":[OSD([subQ0])]}),makeQuery(id+"F5.opFillet","BLEND_FACE",FACE,{"disambiguationData":[OSD([subQ1])]}),makeQuery(id+"F5.opFillet","BLEND_FACE",FACE,{"disambiguationData":[OSD([sQuery(id+"F2.wireOp",EDGE,"E4.top")])]}),makeQuery(id+"F8.opExtrude","SWEPT_FACE",FACE,{"disambiguationData":[OSD([sQuery(id+"F7.wireOp",EDGE,"E5")])]})])],"derivedFrom":makeQuery(id+"F1.opExtrude","CAP_FACE",FACE,{"disambiguationData":[OSD([sQuery(id+"F0.wireOp",EDGE,"E0"),subQ0,subQ1,sQuery(id+"F0.wireOp",EDGE,"E3")])],"isStart":false})});}
            var sketch = newSketch(context, id + "F45", { "sketchPlane" : qUnion([Q0])});
            skLineSegment(sketch, "E60", {"start": v(-16.65, -7.09) * mm, "end": v(-7.18, -7.09) * mm});
            skArc(sketch, "E61", {"start": v(-7.18, -10.19) * mm, "mid": v(-5.63, -8.64) * mm, "end": v(-7.18, -7.09) * mm});
            skLineSegment(sketch, "E62", {"start": v(-7.18, -10.19) * mm, "end": v(-16.6, -10.19) * mm});
            skArc(sketch, "E63", {"start": v(-16.65, -7.09) * mm, "mid": v(-18.15, -8.66) * mm, "end": v(-16.6, -10.19) * mm});
            skCircle(sketch, "E64", {"center": v(-15.43, -8.64) * mm, "radius": 1.23 * mm});
            skCircle(sketch, "E65", {"center": v(-12.3, -8.64) * mm, "radius": 1.33 * mm});
            skCircle(sketch, "E66", {"center": v(-9.18, -8.64) * mm, "radius": 1.25 * mm});
            skSolve(sketch);
        }
        {
            var Q0;
            Q0 = qSketchRegion(id + "F45", true);
            extrude(context, id + "F46", {"entities" : qUnion([Q0]), "operationType" : NewBodyOperationType.REMOVE, "oppositeDirection" : true, "depth" : 3.56 * mm});
        }
        {
            var Q0;
            Q0=makeQuery(id+"F46.boolean.opBoolean","COPY",FACE,{"derivedFrom":makeQuery(id+"F46.opExtrude","CAP_FACE",FACE,{"disambiguationData":[OSD([sQuery(id+"F45.wireOp",EDGE,"E60"),sQuery(id+"F45.wireOp",EDGE,"E61"),sQuery(id+"F45.wireOp",EDGE,"E62"),sQuery(id+"F45.wireOp",EDGE,"E63"),sQuery(id+"F45.wireOp",EDGE,"E64"),sQuery(id+"F45.wireOp",EDGE,"E65"),sQuery(id+"F45.wireOp",EDGE,"E66")])],"isStart":false})});
            extrude(context, id + "F47", {"entities" : qUnion([Q0]), "depth" : 3.8 * mm});
        }
        {
            var Q0;
            {var subQ0=sQuery(id+"F0.wireOp",EDGE,"E1");var subQ1=sQuery(id+"F0.wireOp",EDGE,"E2");Q0=makeQuery(id+"F46.boolean.opBoolean","SPLIT",FACE,{"disambiguationData":[TD([makeQuery(id+"F46.opExtrude","SWEPT_FACE",FACE,{"disambiguationData":[OSD([sQuery(id+"F45.wireOp",EDGE,"E65")])]})])],"derivedFrom":makeQuery(id+"F8.boolean.opBoolean","SPLIT",FACE,{"disambiguationData":[TD([makeQuery(id+"F5.opFillet","BLEND_FACE",FACE,{"disambiguationData":[OSD([subQ0])]}),makeQuery(id+"F5.opFillet","BLEND_FACE",FACE,{"disambiguationData":[OSD([subQ1])]}),makeQuery(id+"F5.opFillet","BLEND_FACE",FACE,{"disambiguationData":[OSD([sQuery(id+"F2.wireOp",EDGE,"E4.top")])]}),makeQuery(id+"F8.opExtrude","SWEPT_FACE",FACE,{"disambiguationData":[OSD([sQuery(id+"F7.wireOp",EDGE,"E5")])]})])],"derivedFrom":makeQuery(id+"F1.opExtrude","CAP_FACE",FACE,{"disambiguationData":[OSD([sQuery(id+"F0.wireOp",EDGE,"E0"),subQ0,subQ1,sQuery(id+"F0.wireOp",EDGE,"E3")])],"isStart":false})})});}
            var sketch = newSketch(context, id + "F48", { "sketchPlane" : qUnion([Q0])});
            skCircle(sketch, "E67", {"center": v(-12.3, -8.64) * mm, "radius": 0.67 * mm});
            skCircle(sketch, "E68", {"center": v(-9.15, -8.7) * mm, "radius": 0.62 * mm});
            skCircle(sketch, "E69", {"center": v(-15.45, -8.6) * mm, "radius": 0.64 * mm});
            skSolve(sketch);
        }
        {
            var Q0;
            Q0 = qSketchRegion(id + "F48", true);
            extrude(context, id + "F49", {"entities" : qUnion([Q0]), "operationType" : NewBodyOperationType.REMOVE, "oppositeDirection" : true, "depth" : 3.56 * mm});
        }
        {
            var Q0;
            Q0=makeQuery(id+"F49.boolean.opBoolean","COPY",FACE,{"derivedFrom":makeQuery(id+"F49.opExtrude","CAP_FACE",FACE,{"disambiguationData":[OSD([sQuery(id+"F48.wireOp",EDGE,"E69")])],"isStart":false})});
            var Q1;
            Q1=makeQuery(id+"F49.boolean.opBoolean","COPY",FACE,{"derivedFrom":makeQuery(id+"F49.opExtrude","CAP_FACE",FACE,{"disambiguationData":[OSD([sQuery(id+"F48.wireOp",EDGE,"E67")])],"isStart":false})});
            var Q2;
            Q2=makeQuery(id+"F49.boolean.opBoolean","COPY",FACE,{"derivedFrom":makeQuery(id+"F49.opExtrude","CAP_FACE",FACE,{"disambiguationData":[OSD([sQuery(id+"F48.wireOp",EDGE,"E68")])],"isStart":false})});
            extrude(context, id + "F50", {"entities" : qUnion([Q0, Q1, Q2]), "depth" : 3.8 * mm});
        }
        {
            var Q0;
            {var subQ0=makeQuery(id+"F5.opFillet","BLEND_FACE",FACE,{"disambiguationData":[OSD([sQuery(id+"F2.wireOp",EDGE,"E4.right")])]});var subQ1=sQuery(id+"F0.wireOp",EDGE,"E2");var subQ2=makeQuery(id+"F5.opFillet","BLEND_FACE",FACE,{"disambiguationData":[OSD([subQ1])]});var subQ3=makeQuery(id+"F5.opFillet","BLEND_FACE",FACE,{"disambiguationData":[OSD([sQuery(id+"F2.wireOp",EDGE,"E4.top")])]});var subQ4=sQuery(id+"F0.wireOp",EDGE,"E0");var subQ5=makeQuery(id+"F5.opFillet","BLEND_FACE",FACE,{"disambiguationData":[OSD([subQ4])]});var subQ6=makeQuery(id+"F8.opExtrude","SWEPT_FACE",FACE,{"disambiguationData":[OSD([sQuery(id+"F7.wireOp",EDGE,"E5")])]});var subQ8=sQuery(id+"F2.wireOp",EDGE,"E4.bottom");var subQ9=makeQuery(id+"F5.opFillet","BLEND_FACE",FACE,{"disambiguationData":[OSD([subQ8])]});var subQ10=sQuery(id+"F0.wireOp",EDGE,"E3");var subQ11=makeQuery(id+"F5.opFillet","BLEND_FACE",FACE,{"disambiguationData":[OSD([subQ10])]});var subQ14=sQuery(id+"F0.wireOp",EDGE,"E1");var subQ15=makeQuery(id+"F1.opExtrude","CAP_FACE",FACE,{"disambiguationData":[OSD([subQ4,subQ14,subQ1,subQ10])],"isStart":false});Q0=makeQuery(id+"F40.boolean.opBoolean","SPLIT",FACE,{"disambiguationData":[TD([subQ2])],"derivedFrom":makeQuery(id+"F37.boolean.opBoolean","SPLIT",FACE,{"disambiguationData":[TD([subQ2])],"derivedFrom":makeQuery(id+"F25.boolean.opBoolean","SPLIT",FACE,{"disambiguationData":[TD([subQ5])],"derivedFrom":makeQuery(id+"F8.boolean.opBoolean","SPLIT",FACE,{"disambiguationData":[TD([subQ5,makeQuery(id+"F5.opFillet","BLEND_FACE",FACE,{"disambiguationData":[OSD([subQ14])]}),subQ2,subQ11,subQ9,subQ3,subQ0,subQ6])],"derivedFrom":subQ15})})})});}
            var sketch = newSketch(context, id + "F51", { "sketchPlane" : qUnion([Q0])});
            skLineSegment(sketch, "E70", {"start": v(10.81, -7.09) * mm, "end": v(18.36, -7.09) * mm});
            skArc(sketch, "E71", {"start": v(18.36, -10.19) * mm, "mid": v(19.92, -8.64) * mm, "end": v(18.36, -7.09) * mm});
            skLineSegment(sketch, "E72", {"start": v(18.36, -10.19) * mm, "end": v(10.81, -10.19) * mm});
            skArc(sketch, "E73", {"start": v(10.81, -7.09) * mm, "mid": v(9.26, -8.64) * mm, "end": v(10.81, -10.19) * mm});
            skCircle(sketch, "E74", {"center": v(11.89, -8.64) * mm, "radius": 0.98 * mm});
            skCircle(sketch, "E75", {"center": v(14.47, -8.64) * mm, "radius": 1.2 * mm});
            skCircle(sketch, "E76", {"center": v(16.98, -8.64) * mm, "radius": 0.95 * mm});
            skSolve(sketch);
        }
        {
            var Q0;
            Q0 = qSketchRegion(id + "F51", true);
            extrude(context, id + "F52", {"entities" : qUnion([Q0]), "operationType" : NewBodyOperationType.REMOVE, "oppositeDirection" : true, "depth" : 3.56 * mm});
        }
        {
            var Q0;
            Q0=makeQuery(id+"F52.boolean.opBoolean","COPY",FACE,{"derivedFrom":makeQuery(id+"F52.opExtrude","CAP_FACE",FACE,{"disambiguationData":[OSD([sQuery(id+"F51.wireOp",EDGE,"E70"),sQuery(id+"F51.wireOp",EDGE,"E71"),sQuery(id+"F51.wireOp",EDGE,"E72"),sQuery(id+"F51.wireOp",EDGE,"E73"),sQuery(id+"F51.wireOp",EDGE,"E74"),sQuery(id+"F51.wireOp",EDGE,"E75"),sQuery(id+"F51.wireOp",EDGE,"E76")])],"isStart":false})});
            extrude(context, id + "F53", {"entities" : qUnion([Q0]), "depth" : 3.8 * mm});
        }
        {
            var Q0;
            {var subQ0=makeQuery(id+"F5.opFillet","BLEND_FACE",FACE,{"disambiguationData":[OSD([sQuery(id+"F2.wireOp",EDGE,"E4.right")])]});var subQ1=sQuery(id+"F0.wireOp",EDGE,"E2");var subQ2=makeQuery(id+"F5.opFillet","BLEND_FACE",FACE,{"disambiguationData":[OSD([subQ1])]});var subQ3=makeQuery(id+"F5.opFillet","BLEND_FACE",FACE,{"disambiguationData":[OSD([sQuery(id+"F2.wireOp",EDGE,"E4.top")])]});var subQ4=sQuery(id+"F0.wireOp",EDGE,"E0");var subQ5=makeQuery(id+"F5.opFillet","BLEND_FACE",FACE,{"disambiguationData":[OSD([subQ4])]});var subQ6=makeQuery(id+"F8.opExtrude","SWEPT_FACE",FACE,{"disambiguationData":[OSD([sQuery(id+"F7.wireOp",EDGE,"E5")])]});var subQ8=sQuery(id+"F2.wireOp",EDGE,"E4.bottom");var subQ9=makeQuery(id+"F5.opFillet","BLEND_FACE",FACE,{"disambiguationData":[OSD([subQ8])]});var subQ10=sQuery(id+"F0.wireOp",EDGE,"E3");var subQ11=makeQuery(id+"F5.opFillet","BLEND_FACE",FACE,{"disambiguationData":[OSD([subQ10])]});var subQ14=sQuery(id+"F0.wireOp",EDGE,"E1");var subQ15=makeQuery(id+"F1.opExtrude","CAP_FACE",FACE,{"disambiguationData":[OSD([subQ4,subQ14,subQ1,subQ10])],"isStart":false});Q0=makeQuery(id+"F52.boolean.opBoolean","SPLIT",FACE,{"disambiguationData":[TD([makeQuery(id+"F52.opExtrude","SWEPT_FACE",FACE,{"disambiguationData":[OSD([sQuery(id+"F51.wireOp",EDGE,"E75")])]})])],"derivedFrom":makeQuery(id+"F40.boolean.opBoolean","SPLIT",FACE,{"disambiguationData":[TD([subQ2])],"derivedFrom":makeQuery(id+"F37.boolean.opBoolean","SPLIT",FACE,{"disambiguationData":[TD([subQ2])],"derivedFrom":makeQuery(id+"F25.boolean.opBoolean","SPLIT",FACE,{"disambiguationData":[TD([subQ5])],"derivedFrom":makeQuery(id+"F8.boolean.opBoolean","SPLIT",FACE,{"disambiguationData":[TD([subQ5,makeQuery(id+"F5.opFillet","BLEND_FACE",FACE,{"disambiguationData":[OSD([subQ14])]}),subQ2,subQ11,subQ9,subQ3,subQ0,subQ6])],"derivedFrom":subQ15})})})})});}
            var sketch = newSketch(context, id + "F54", { "sketchPlane" : qUnion([Q0])});
            skCircle(sketch, "E77", {"center": v(14.47, -8.64) * mm, "radius": 0.61 * mm});
            skCircle(sketch, "E78", {"center": v(11.94, -8.7) * mm, "radius": 0.57 * mm});
            skCircle(sketch, "E79", {"center": v(17.06, -8.56) * mm, "radius": 0.55 * mm});
            skSolve(sketch);
        }
        {
            var Q0;
            Q0 = qSketchRegion(id + "F54", true);
            extrude(context, id + "F55", {"entities" : qUnion([Q0]), "operationType" : NewBodyOperationType.REMOVE, "oppositeDirection" : true, "depth" : 3.56 * mm});
        }
        {
            var Q0;
            Q0=makeQuery(id+"F55.boolean.opBoolean","COPY",FACE,{"derivedFrom":makeQuery(id+"F55.opExtrude","CAP_FACE",FACE,{"disambiguationData":[OSD([sQuery(id+"F54.wireOp",EDGE,"E78")])],"isStart":false})});
            var Q1;
            Q1=makeQuery(id+"F55.boolean.opBoolean","COPY",FACE,{"derivedFrom":makeQuery(id+"F55.opExtrude","CAP_FACE",FACE,{"disambiguationData":[OSD([sQuery(id+"F54.wireOp",EDGE,"E77")])],"isStart":false})});
            var Q2;
            Q2=makeQuery(id+"F55.boolean.opBoolean","COPY",FACE,{"derivedFrom":makeQuery(id+"F55.opExtrude","CAP_FACE",FACE,{"disambiguationData":[OSD([sQuery(id+"F54.wireOp",EDGE,"E79")])],"isStart":false})});
            extrude(context, id + "F56", {"entities" : qUnion([Q0, Q1, Q2]), "depth" : 3.56 * mm});
        }
        {
            var Q0;
            {var subQ0=makeQuery(id+"F5.opFillet","BLEND_FACE",FACE,{"disambiguationData":[OSD([sQuery(id+"F2.wireOp",EDGE,"E4.right")])]});var subQ1=sQuery(id+"F0.wireOp",EDGE,"E2");var subQ2=makeQuery(id+"F5.opFillet","BLEND_FACE",FACE,{"disambiguationData":[OSD([subQ1])]});var subQ3=makeQuery(id+"F5.opFillet","BLEND_FACE",FACE,{"disambiguationData":[OSD([sQuery(id+"F2.wireOp",EDGE,"E4.top")])]});var subQ4=sQuery(id+"F0.wireOp",EDGE,"E0");var subQ5=makeQuery(id+"F5.opFillet","BLEND_FACE",FACE,{"disambiguationData":[OSD([subQ4])]});var subQ9=makeQuery(id+"F8.opExtrude","SWEPT_FACE",FACE,{"disambiguationData":[OSD([sQuery(id+"F7.wireOp",EDGE,"E5")])]});var subQ11=sQuery(id+"F2.wireOp",EDGE,"E4.bottom");var subQ12=makeQuery(id+"F5.opFillet","BLEND_FACE",FACE,{"disambiguationData":[OSD([subQ11])]});var subQ13=sQuery(id+"F0.wireOp",EDGE,"E3");var subQ14=makeQuery(id+"F5.opFillet","BLEND_FACE",FACE,{"disambiguationData":[OSD([subQ13])]});var subQ17=sQuery(id+"F0.wireOp",EDGE,"E1");var subQ18=makeQuery(id+"F1.opExtrude","CAP_FACE",FACE,{"disambiguationData":[OSD([subQ4,subQ17,subQ1,subQ13])],"isStart":false});Q0=makeQuery(id+"F52.boolean.opBoolean","SPLIT",FACE,{"disambiguationData":[TD([subQ5])],"derivedFrom":makeQuery(id+"F40.boolean.opBoolean","SPLIT",FACE,{"disambiguationData":[TD([subQ2])],"derivedFrom":makeQuery(id+"F37.boolean.opBoolean","SPLIT",FACE,{"disambiguationData":[TD([subQ2])],"derivedFrom":makeQuery(id+"F25.boolean.opBoolean","SPLIT",FACE,{"disambiguationData":[TD([subQ5])],"derivedFrom":makeQuery(id+"F8.boolean.opBoolean","SPLIT",FACE,{"disambiguationData":[TD([subQ5,makeQuery(id+"F5.opFillet","BLEND_FACE",FACE,{"disambiguationData":[OSD([subQ17])]}),subQ2,subQ14,subQ12,subQ3,subQ0,subQ9])],"derivedFrom":subQ18})})})})});}
            var sketch = newSketch(context, id + "F57", { "sketchPlane" : qUnion([Q0])});
            skCircle(sketch, "E80", {"center": v(23.4, -8.68) * mm, "radius": 1.74 * mm});
            skSolve(sketch);
        }
        {
            var Q0;
            {var subQ0=sQuery(id+"F57.wireOp",EDGE,"E80");var subQ1=makeQuery(id+"F1.opExtrude","CAP_FACE",FACE,{"disambiguationData":[OSD([sQuery(id+"F0.wireOp",EDGE,"E0"),sQuery(id+"F0.wireOp",EDGE,"E1"),sQuery(id+"F0.wireOp",EDGE,"E2"),sQuery(id+"F0.wireOp",EDGE,"E3")])],"isStart":false});var subQ2=makeQuery(id+"F5.opFillet","BLEND_FACE",FACE,{"disambiguationData":[OSD([sQuery(id+"F2.wireOp",EDGE,"E4.right")])]});var subQ3=sQuery(id+"F2.wireOp",EDGE,"E4.top");var subQ5=makeQuery(id+"F52.boolean.opBoolean","SPLIT",EDGE,{"disambiguationData":[TD([subQ2])],"derivedFrom":makeQuery(id+"F8.boolean.opBoolean","SPLIT",EDGE,{"disambiguationData":[TD([subQ2])],"derivedFrom":makeQuery(id+"F5.opFillet","BLEND_EDGE",EDGE,{"blendedFrom":[makeQuery(id+"F3.boolean.opBoolean","COPY",EDGE,{"derivedFrom":makeQuery(id+"F3.opExtrude","CAP_EDGE",EDGE,{"disambiguationData":[OSD([subQ3])],"isStart":true})}),subQ1],"blendedInto":[subQ1]})})});var subQ6=makeQuery(id+"F57.imprint","INTERSECT",VERTEX,{"disambiguationData":[OD(0.0)],"derivedFrom":[subQ5,subQ0]});Q0=makeQuery(id+"F57.imprint","IMPRINT",FACE,{"disambiguationData":[TD([[makeQuery(id+"F57.imprint","IMPRINT",EDGE,{"disambiguationData":[TD([[subQ6,1.0]])],"derivedFrom":subQ0}),1.0]])]});}
            var Q1;
            {var subQ0=sQuery(id+"F57.wireOp",EDGE,"E80");var subQ1=sQuery(id+"F0.wireOp",EDGE,"E2");var subQ3=sQuery(id+"F0.wireOp",EDGE,"E0");var subQ4=makeQuery(id+"F5.opFillet","BLEND_FACE",FACE,{"disambiguationData":[OSD([subQ3])]});var subQ5=makeQuery(id+"F1.opExtrude","CAP_FACE",FACE,{"disambiguationData":[OSD([subQ3,sQuery(id+"F0.wireOp",EDGE,"E1"),subQ1,sQuery(id+"F0.wireOp",EDGE,"E3")])],"isStart":false});var subQ6=makeQuery(id+"F52.boolean.opBoolean","SPLIT",EDGE,{"disambiguationData":[TD([subQ4])],"derivedFrom":makeQuery(id+"F8.boolean.opBoolean","SPLIT",EDGE,{"disambiguationData":[TD([subQ4])],"derivedFrom":makeQuery(id+"F5.opFillet","BLEND_EDGE",EDGE,{"blendedFrom":[makeQuery(id+"F1.opExtrude","CAP_EDGE",EDGE,{"disambiguationData":[OSD([subQ1])],"isStart":false}),subQ5],"blendedInto":[subQ5]})})});var subQ7=makeQuery(id+"F57.imprint","INTERSECT",VERTEX,{"disambiguationData":[OD(0.0)],"derivedFrom":[subQ6,subQ0]});Q1=makeQuery(id+"F57.imprint","IMPRINT",FACE,{"disambiguationData":[TD([[makeQuery(id+"F57.imprint","IMPRINT",EDGE,{"disambiguationData":[TD([[subQ7,-1.0]])],"derivedFrom":subQ0}),1.0]])]});}
            var Q2;
            {var subQ0=sQuery(id+"F57.wireOp",EDGE,"E80");var subQ1=sQuery(id+"F0.wireOp",EDGE,"E2");var subQ2=sQuery(id+"F0.wireOp",EDGE,"E0");var subQ3=makeQuery(id+"F1.opExtrude","CAP_FACE",FACE,{"disambiguationData":[OSD([subQ2,sQuery(id+"F0.wireOp",EDGE,"E1"),subQ1,sQuery(id+"F0.wireOp",EDGE,"E3")])],"isStart":false});var subQ4=makeQuery(id+"F5.opFillet","BLEND_FACE",FACE,{"disambiguationData":[OSD([sQuery(id+"F2.wireOp",EDGE,"E4.right")])]});var subQ5=sQuery(id+"F2.wireOp",EDGE,"E4.top");var subQ9=subQ3;var subQ10=makeQuery(id+"F52.boolean.opBoolean","SPLIT",EDGE,{"disambiguationData":[TD([subQ4])],"derivedFrom":makeQuery(id+"F8.boolean.opBoolean","SPLIT",EDGE,{"disambiguationData":[TD([subQ4])],"derivedFrom":makeQuery(id+"F5.opFillet","BLEND_EDGE",EDGE,{"blendedFrom":[makeQuery(id+"F3.boolean.opBoolean","COPY",EDGE,{"derivedFrom":makeQuery(id+"F3.opExtrude","CAP_EDGE",EDGE,{"disambiguationData":[OSD([subQ5])],"isStart":true})}),subQ9],"blendedInto":[subQ9]})})});var subQ11=makeQuery(id+"F57.imprint","INTERSECT",VERTEX,{"disambiguationData":[OD(0.0)],"derivedFrom":[subQ10,subQ0]});Q2=makeQuery(id+"F57.imprint","IMPRINT",FACE,{"disambiguationData":[TD([[makeQuery(id+"F57.imprint","IMPRINT",EDGE,{"disambiguationData":[TD([[subQ11,-1.0]])],"derivedFrom":subQ0}),1.0]])]});}
            extrude(context, id + "F58", {"entities" : qUnion([Q0, Q1, Q2]), "operationType" : NewBodyOperationType.REMOVE, "oppositeDirection" : true, "depth" : 3.56 * mm});
        }
        {
            var Q0;
            Q0=makeQuery(id+"F58.boolean.opBoolean","COPY",FACE,{"derivedFrom":makeQuery(id+"F58.opExtrude","CAP_FACE",FACE,{"disambiguationData":[OSD([sQuery(id+"F57.wireOp",EDGE,"E80")])],"isStart":false})});
            extrude(context, id + "F59", {"entities" : qUnion([Q0]), "depth" : 2.54 * mm});
        }
        {
            var Q0;
            Q0=makeQuery(id+"F59.opExtrude","CAP_FACE",FACE,{"disambiguationData":[OSD([sQuery(id+"F57.wireOp",EDGE,"E80")])],"isStart":false});
            var sketch = newSketch(context, id + "F60", { "sketchPlane" : qUnion([Q0])});
            skCircle(sketch, "E81", {"center": v(23.4, -8.68) * mm, "radius": 0.42 * mm});
            skSolve(sketch);
        }
        {
            var Q0;
            Q0 = qSketchRegion(id + "F60", true);
            extrude(context, id + "F61", {"entities" : qUnion([Q0]), "operationType" : NewBodyOperationType.REMOVE, "oppositeDirection" : true, "depth" : 3.05 * mm});
        }
    });
